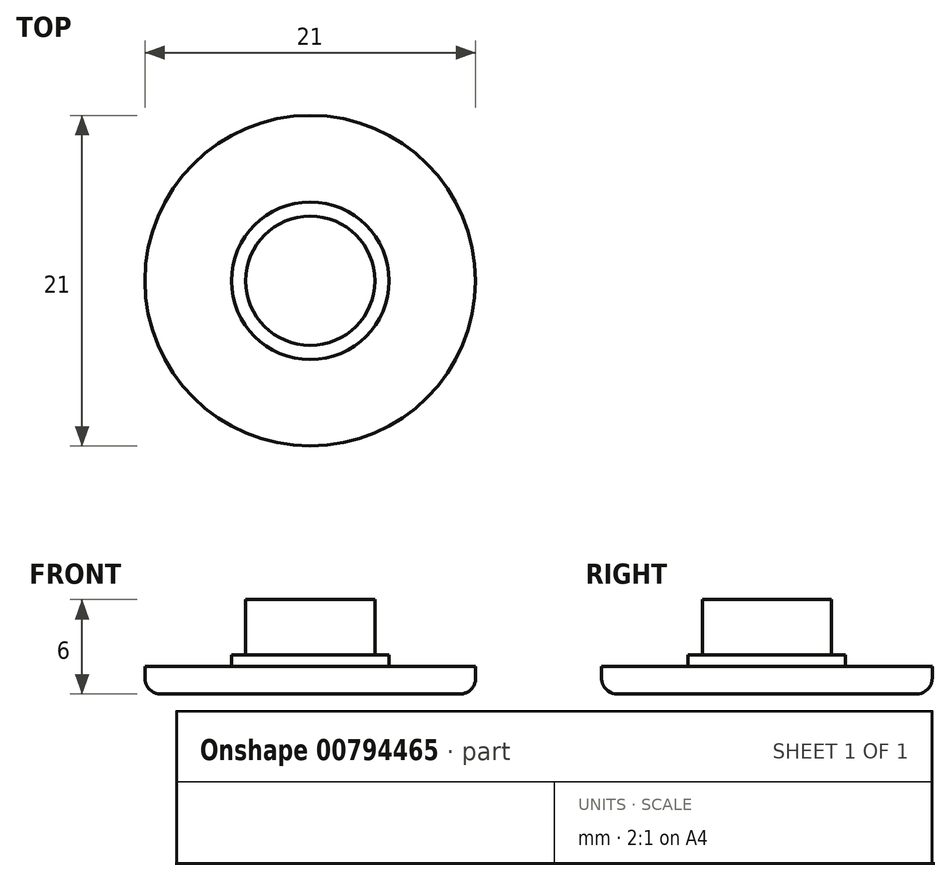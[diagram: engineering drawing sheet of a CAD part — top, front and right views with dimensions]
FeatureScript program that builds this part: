
annotation { "Feature Type Name" : "Feature", "Feature Type Description" : "" }
export const myFeature = defineFeature(function(context is Context, id is Id, definition is map)
    precondition{}
    {
        {
            var Q0;
            Q0=qCreatedBy(makeId("Top.planeOp"),FACE);
            var sketch = newSketch(context, id + "F0", { "sketchPlane" : qUnion([Q0])});
            skCircle(sketch, "E0", {"center": v(0, 0) * mm, "radius": 10.5 * mm});
            skPoint(sketch, "E1", {"position": v(10.5, 0) * mm});
            skCircle(sketch, "E2", {"center": v(0, 0) * mm, "radius": 4.1 * mm});
            skPoint(sketch, "E3", {"position": v(4.1, 0) * mm});
            skCircle(sketch, "E4", {"center": v(0, 0) * mm, "radius": 5 * mm});
            skPoint(sketch, "E5", {"position": v(5, 0) * mm});
            skSolve(sketch);
        }
        {
            var Q0;
            Q0=makeQuery(id+"F0.imprint","IMPRINT",FACE,{"disambiguationData":[TD([[makeQuery(id+"F0.imprint","IMPRINT",EDGE,{"derivedFrom":sQuery(id+"F0.wireOp",EDGE,"E0")}),1.0]])]});
            extrude(context, id + "F1", {"entities" : qUnion([Q0]), "depth" : 1.75 * mm, "offsetDistance" : 25 * mm});
        }
        {
            var Q0;
            Q0=makeQuery(id+"F0.imprint","IMPRINT",FACE,{"disambiguationData":[TD([[makeQuery(id+"F0.imprint","IMPRINT",EDGE,{"derivedFrom":sQuery(id+"F0.wireOp",EDGE,"E2")}),1.0]])]});
            extrude(context, id + "F2", {"entities" : qUnion([Q0]), "operationType" : NewBodyOperationType.ADD, "depth" : 6 * mm, "offsetDistance" : 25 * mm});
        }
        {
            var Q0;
            Q0=makeQuery(id+"F0.imprint","IMPRINT",FACE,{"disambiguationData":[TD([[makeQuery(id+"F0.imprint","IMPRINT",EDGE,{"derivedFrom":sQuery(id+"F0.wireOp",EDGE,"E2")}),-1.0]])]});
            extrude(context, id + "F3", {"entities" : qUnion([Q0]), "depth" : 2.5 * mm, "offsetDistance" : 25 * mm});
        }
        {
            var Q0;
            Q0=makeQuery(id+"F1.opExtrude","SWEPT_BODY",BODY,{"disambiguationData":[OSD([sQuery(id+"F0.wireOp",EDGE,"E0"),sQuery(id+"F0.wireOp",EDGE,"E4")])]});
            var Q1;
            Q1=makeQuery(id+"F3.opExtrude","SWEPT_BODY",BODY,{"disambiguationData":[OSD([sQuery(id+"F0.wireOp",EDGE,"E2"),sQuery(id+"F0.wireOp",EDGE,"E4")])]});
            var Q2;
            Q2=makeQuery(id+"F2.opExtrude","SWEPT_BODY",BODY,{"disambiguationData":[OSD([sQuery(id+"F0.wireOp",EDGE,"E2")])]});
            booleanBodies(context, id + "F4", {"operationType" : BooleanOperationType.UNION, "tools" : qUnion([Q0, Q1, Q2])});
        }
        {
            var Q0;
            Q0=makeQuery(id+"F1.opExtrude","CAP_EDGE",EDGE,{"disambiguationData":[OSD([sQuery(id+"F0.wireOp",EDGE,"E0")])],"isStart":true});
            var Q1;
            {var subQ0=sQuery(id+"F0.wireOp",EDGE,"E4");var subQ1=sQuery(id+"F0.wireOp",EDGE,"E2");Q1=makeQuery(id+"F4.opBoolean","MERGE",FACE,{"derivedFrom":[makeQuery(id+"F1.opExtrude","CAP_FACE",FACE,{"disambiguationData":[OSD([sQuery(id+"F0.wireOp",EDGE,"E0"),subQ0])],"isStart":true}),makeQuery(id+"F2.opExtrude","CAP_FACE",FACE,{"disambiguationData":[OSD([subQ1])],"isStart":true}),makeQuery(id+"F3.opExtrude","CAP_FACE",FACE,{"disambiguationData":[OSD([subQ1,subQ0])],"isStart":true})]});}
            fillet(context, id + "F5", {"entities" : qUnion([Q0, Q1]), "radius" : 1 * mm, "tangentPropagation" : true, "allowEdgeOverflow" : false});
        }
    });
